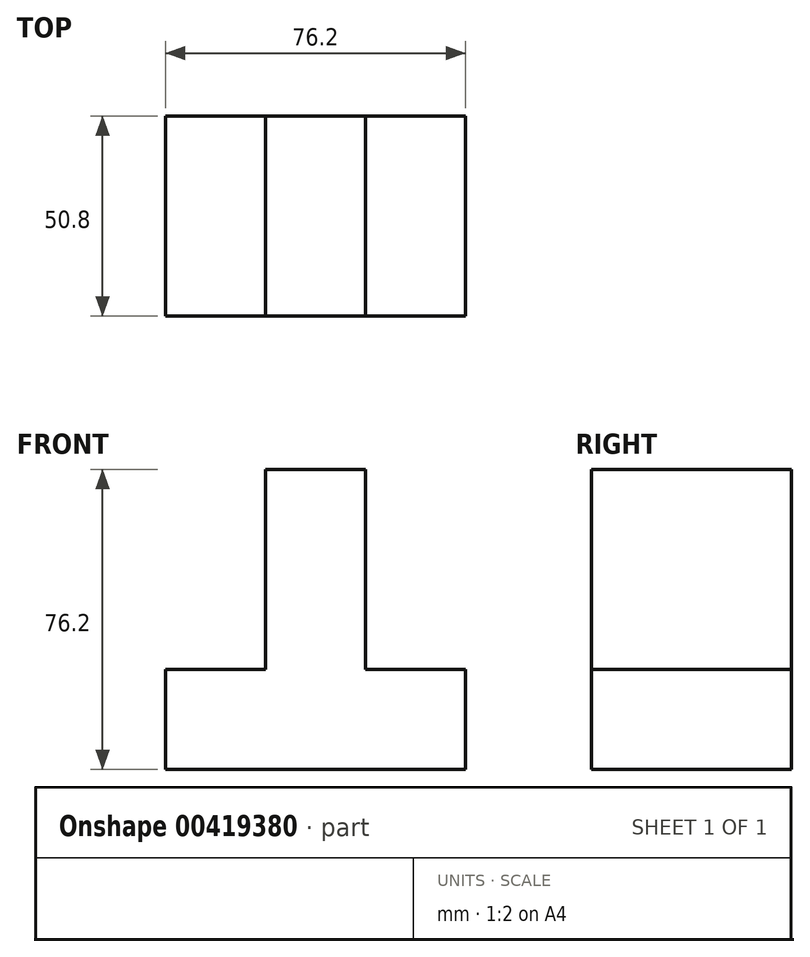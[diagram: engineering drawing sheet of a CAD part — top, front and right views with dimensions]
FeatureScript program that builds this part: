
annotation { "Feature Type Name" : "Feature", "Feature Type Description" : "" }
export const myFeature = defineFeature(function(context is Context, id is Id, definition is map)
    precondition{}
    {
        {
            var Q0;
            Q0=qCreatedBy(makeId("Front.planeOp"),FACE);
            var sketch = newSketch(context, id + "F0", { "sketchPlane" : qUnion([Q0])});
            skLineSegment(sketch, "E0", {"start": v(0, 0) * mm, "end": v(76.2, 0) * mm});
            skLineSegment(sketch, "E1", {"start": v(0, 0) * mm, "end": v(0, 25.4) * mm});
            skLineSegment(sketch, "E2", {"start": v(0, 25.4) * mm, "end": v(25.4, 25.4) * mm});
            skLineSegment(sketch, "E3", {"start": v(25.4, 25.4) * mm, "end": v(25.4, 76.2) * mm});
            skLineSegment(sketch, "E4", {"start": v(25.4, 76.2) * mm, "end": v(50.8, 76.2) * mm});
            skLineSegment(sketch, "E5", {"start": v(50.8, 76.2) * mm, "end": v(50.8, 25.4) * mm});
            skLineSegment(sketch, "E6", {"start": v(50.8, 25.4) * mm, "end": v(76.2, 25.4) * mm});
            skLineSegment(sketch, "E7", {"start": v(76.2, 25.4) * mm, "end": v(76.2, 0) * mm});
            skSolve(sketch);
        }
        {
            var Q0;
            Q0 = qSketchRegion(id + "F0", true);
            extrude(context, id + "F1", {"entities" : qUnion([Q0]), "depth" : 50.8 * mm});
        }
    });
